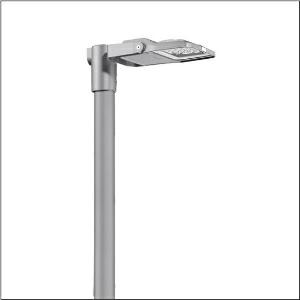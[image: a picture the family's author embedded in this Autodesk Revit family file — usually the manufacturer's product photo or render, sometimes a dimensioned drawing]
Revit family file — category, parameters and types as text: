
# Revit family: floodlight_fl_21_iq_micro___pl64_5xa7761a2e3a_b98d
name_source: partatom
category: Lighting Fixtures
units: mm (PartAtom-declared; Revit-internal decimal feet)

## family parameters
Cut with Voids When Loaded = No
Host = Face
Light Source = No
Part Type = Normal
Room Calculation Point = No
Round Connector Dimension = Use Diameter
Shared = No

## types (1)
- --- (1 x LED, 2870 lm, 23.1 W, 3000K)
    Apparent Load = 23 VA
    CIE Flux Codes = 28 80 98 100 100
    Color Rendering = 70
    Color Temperature = 3000K
    Default Elevation = 1800 mm
    Description = Floodlight FL 21 iQ micro, floodlight, primary light control with lens, of PMMA, primary optical cover: protective disc, of toughened safety glass, transparent, light distribution: PL64, light emission: direct distribution, installation type: surface-mounted, LED, High Power LED, rated luminous flux: 2.870lm, luminous efficacy: 124lm/W, light colour: 730, colour temperature: 3000K, control: optimised constant luminous flux control (CLO 2.0), Desk-Remote (wireless, voltage-free reading and setting of iQ features in the workshop via application-optimized NFC function/RFID function), Light-Fading, Smart-Wire, Night-Set, Lumen-Switch, Temp-Guard, Auto-Match, with terminal, 6-pole, mains connection: 220..240V, AC, 50/60Hz, start of lifetime: 23W, end of service life: 24W, reduction: 11W, luminaire housing, of diecast aluminium, powder-coated, Siteco® metallic grey (DB 702S), corrosivity category C5 mid according to DIN EN ISO 12944, sealing non-destructively replaceable, please order mast flange separately, mast bracket, of steel, galvanised, powder-coated, Siteco® metallic grey (DB 702S), protection rating (complete): IP66, insulation class (complete): insulation class II (safety insulation), certification: CE, ENEC, VDE, protection symbol: D, impact resistance: IK07, permissible operating ambient temperature: -40..+40°C, permissible operating ambient temperature for outdoor applications: -40..+50°C, standard: DIN EN 12944, LABS conformity tested according to VDMA 24364:2018-05, packaging unit: 1 piece

Light Distribution: PL64
    Height = 65 mm
    Lamp = 1 x LED
    Lamp Light Flux = 2870 lm
    Lamp Power = 23.1 W
    Lamp count = 1
    Length = 312 mm
    Luminous efficacy = 124 lm/W
    Manufacturer = Siteco
    ModVariant = No
    Model = 5XA7761A2E3A
    Number of Poles = 1
    OnlyDefault = Yes
    Power Factor = 1
    Product Name = Floodlight FL 21 iQ micro | PL64
    Product group = floodlight | pylon top
    ProductGroupID = 6101
    Protection Class = Protection class II
    Protection Degree = IP 66
    RLX_Detail_Level = 1
    RLX_Emergency_Light_Flux = 0 lm
    RLX_Emergency_Type = 0
    RLX_Emergency_Type_DB = No
    RlxData = <blob elided: 101741 chars, md5=8d2ec67a>
    Socket = socket
    Standby Power = 0 W
    System Light Flux = 2870 lm
    System Power = 23 W
    Type Comments = factory setting: luminous flux: 100 % | dim-lin: 254 | 455 mA
    Type Image = l_1007121.jpg
    URL = http://relux.com
    VarID = @adj_152367
    Voltage = 0 V
    Weight = 0.00 kg
    Width = 230 mm

## geometry (parser evidence)
native form markers: Blend x4, Sweep x13
no freeform markers — native parametric forms only
